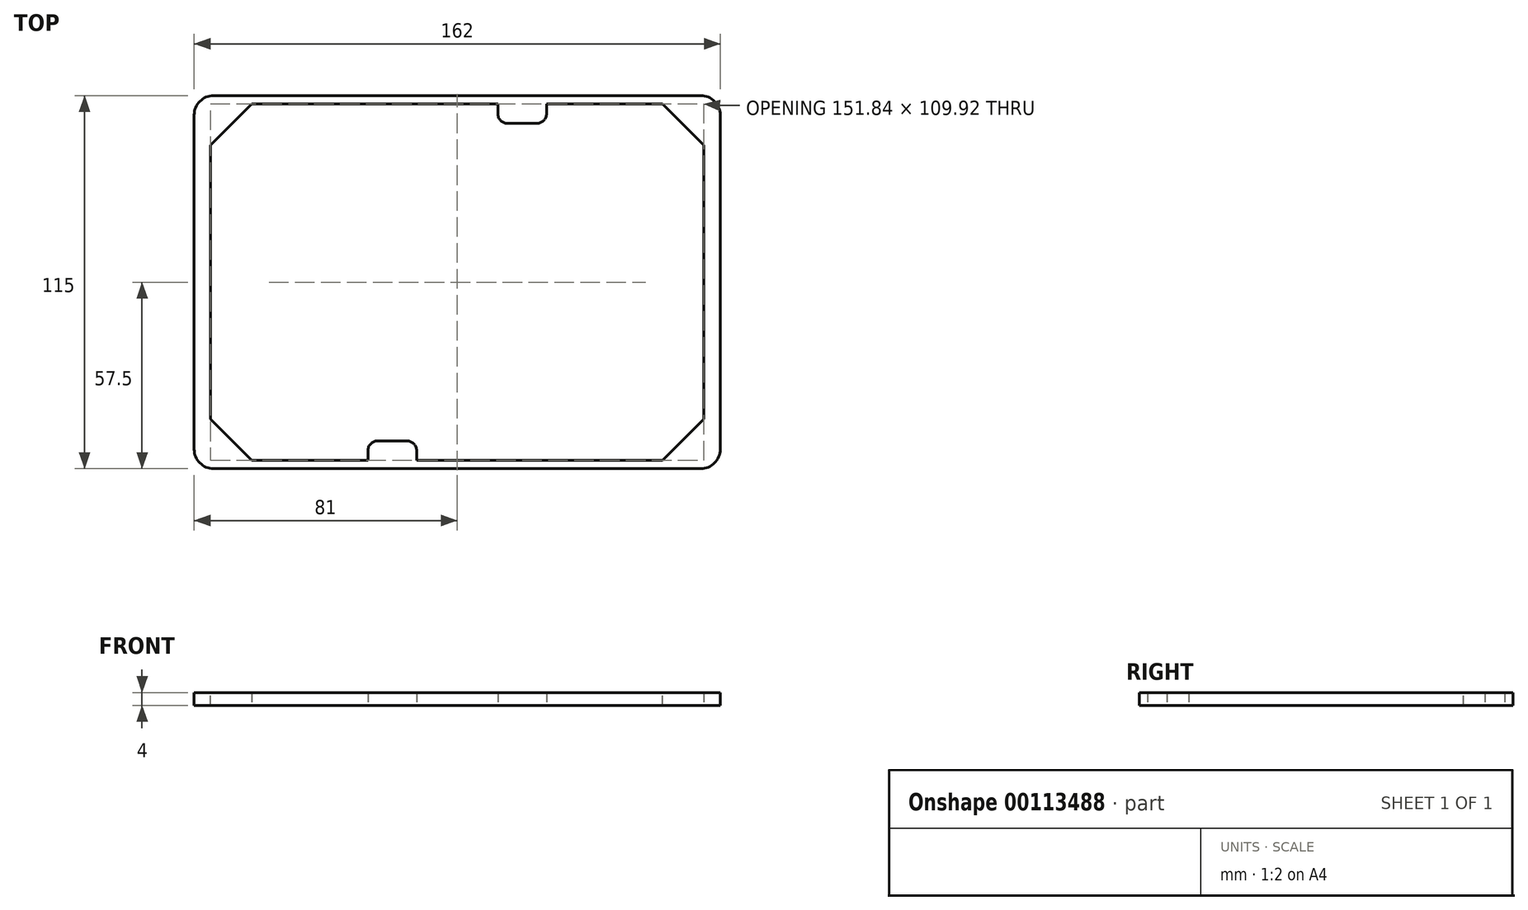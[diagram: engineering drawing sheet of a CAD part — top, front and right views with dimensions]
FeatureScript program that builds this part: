
annotation { "Feature Type Name" : "Feature", "Feature Type Description" : "" }
export const myFeature = defineFeature(function(context is Context, id is Id, definition is map)
    precondition{}
    {
        {
            var Q0;
            Q0=qCreatedBy(makeId("Top.planeOp"),FACE);
            var sketch = newSketch(context, id + "F0", { "sketchPlane" : qUnion([Q0])});
            skLineSegment(sketch, "E0.bottom", {"start": v(0, 0) * mm, "end": v(162, 0) * mm});
            skLineSegment(sketch, "E0.top", {"start": v(0, 115) * mm, "end": v(162, 115) * mm});
            skLineSegment(sketch, "E0.left", {"start": v(0, 0) * mm, "end": v(0, 115) * mm});
            skLineSegment(sketch, "E0.right", {"start": v(162, 0) * mm, "end": v(162, 115) * mm});
            skLineSegment(sketch, "E1.bottom", {"start": v(5.08, 112.46) * mm, "end": v(156.92, 112.46) * mm});
            skLineSegment(sketch, "E1.top", {"start": v(5.08, 2.54) * mm, "end": v(156.92, 2.54) * mm});
            skLineSegment(sketch, "E1.left", {"start": v(5.08, 112.46) * mm, "end": v(5.08, 2.54) * mm});
            skLineSegment(sketch, "E1.right", {"start": v(156.92, 112.46) * mm, "end": v(156.92, 2.54) * mm});
            skSolve(sketch);
        }
        {
            var Q0;
            Q0=qSketchRegion(id+"F0",true);
            extrude(context, id + "F1", {"entities" : qUnion([Q0]), "depth" : 4 * mm});
        }
        {
            var Q0;
            Q0=makeQuery(id+"F1.opExtrude","SWEPT_EDGE",EDGE,{"disambiguationData":[OSD([sQuery(id+"F0.wireOp",EDGE,"E0.top"),sQuery(id+"F0.wireOp",EDGE,"E0.left")])]});
            var Q1;
            Q1=makeQuery(id+"F1.opExtrude","SWEPT_EDGE",EDGE,{"disambiguationData":[OSD([sQuery(id+"F0.wireOp",EDGE,"E0.top"),sQuery(id+"F0.wireOp",EDGE,"E0.right")])]});
            var Q2;
            Q2=makeQuery(id+"F1.opExtrude","SWEPT_EDGE",EDGE,{"disambiguationData":[OSD([sQuery(id+"F0.wireOp",EDGE,"E0.bottom"),sQuery(id+"F0.wireOp",EDGE,"E0.right")])]});
            var Q3;
            Q3=makeQuery(id+"F1.opExtrude","SWEPT_EDGE",EDGE,{"disambiguationData":[OSD([sQuery(id+"F0.wireOp",EDGE,"E0.bottom"),sQuery(id+"F0.wireOp",EDGE,"E0.left")])]});
            fillet(context, id + "F2", {"entities" : qUnion([Q0, Q1, Q2, Q3]), "radius" : 6 * mm, "tangentPropagation" : true, "defaultsChanged" : false, "vertexSettings" : [], "allowEdgeOverflow" : false});
        }
        {
            var Q0;
            Q0=makeQuery(id+"F1.opExtrude","SWEPT_EDGE",EDGE,{"disambiguationData":[OSD([sQuery(id+"F0.wireOp",EDGE,"E1.bottom"),sQuery(id+"F0.wireOp",EDGE,"E1.left")])]});
            var Q1;
            Q1=makeQuery(id+"F1.opExtrude","SWEPT_EDGE",EDGE,{"disambiguationData":[OSD([sQuery(id+"F0.wireOp",EDGE,"E1.top"),sQuery(id+"F0.wireOp",EDGE,"E1.right")])]});
            var Q2;
            Q2=makeQuery(id+"F1.opExtrude","SWEPT_EDGE",EDGE,{"disambiguationData":[OSD([sQuery(id+"F0.wireOp",EDGE,"E1.bottom"),sQuery(id+"F0.wireOp",EDGE,"E1.right")])]});
            var Q3;
            Q3=makeQuery(id+"F1.opExtrude","SWEPT_EDGE",EDGE,{"disambiguationData":[OSD([sQuery(id+"F0.wireOp",EDGE,"E1.top"),sQuery(id+"F0.wireOp",EDGE,"E1.left")])]});
            chamfer(context, id + "F3", {"entities" : qUnion([Q0, Q1, Q2, Q3]), "width" : 12.7 * mm, "tangentPropagation" : true});
        }
        {
            var Q0;
            Q0=makeQuery(id+"F1.opExtrude","SWEPT_FACE",FACE,{"disambiguationData":[OSD([sQuery(id+"F0.wireOp",EDGE,"E1.top")])]});
            var sketch = newSketch(context, id + "F4", { "sketchPlane" : qUnion([Q0])});
            skLineSegment(sketch, "E2.bottom", {"start": v(-68.5, 4) * mm, "end": v(-53.5, 4) * mm});
            skLineSegment(sketch, "E2.top", {"start": v(-68.5, 0) * mm, "end": v(-53.5, 0) * mm});
            skLineSegment(sketch, "E2.left", {"start": v(-68.5, 4) * mm, "end": v(-68.5, 0) * mm});
            skLineSegment(sketch, "E2.right", {"start": v(-53.5, 4) * mm, "end": v(-53.5, 0) * mm});
            skSolve(sketch);
        }
        {
            var Q0;
            Q0 = qSketchRegion(id + "F4", true);
            extrude(context, id + "F5", {"entities" : qUnion([Q0]), "operationType" : NewBodyOperationType.ADD, "depth" : 6 * mm, "offsetDistance" : 25 * mm});
        }
        {
            var Q0;
            Q0=makeQuery(id+"F1.opExtrude","SWEPT_FACE",FACE,{"disambiguationData":[OSD([sQuery(id+"F0.wireOp",EDGE,"E1.bottom")])]});
            var sketch = newSketch(context, id + "F6", { "sketchPlane" : qUnion([Q0])});
            skLineSegment(sketch, "E3.bottom", {"start": v(93.5, 4) * mm, "end": v(108.5, 4) * mm});
            skLineSegment(sketch, "E3.top", {"start": v(93.5, 0) * mm, "end": v(108.5, 0) * mm});
            skLineSegment(sketch, "E3.left", {"start": v(93.5, 4) * mm, "end": v(93.5, 0) * mm});
            skLineSegment(sketch, "E3.right", {"start": v(108.5, 4) * mm, "end": v(108.5, 0) * mm});
            skSolve(sketch);
        }
        {
            var Q0;
            Q0 = qSketchRegion(id + "F6", true);
            extrude(context, id + "F7", {"entities" : qUnion([Q0]), "operationType" : NewBodyOperationType.ADD, "depth" : 6 * mm, "offsetDistance" : 25 * mm});
        }
        {
            var Q0;
            Q0=makeQuery(id+"F7.opExtrude","CAP_EDGE",EDGE,{"disambiguationData":[OSD([sQuery(id+"F6.wireOp",EDGE,"E3.left")])],"isStart":false});
            var Q1;
            Q1=makeQuery(id+"F7.opExtrude","CAP_EDGE",EDGE,{"disambiguationData":[OSD([sQuery(id+"F6.wireOp",EDGE,"E3.right")])],"isStart":false});
            var Q2;
            Q2=makeQuery(id+"F5.opExtrude","CAP_EDGE",EDGE,{"disambiguationData":[OSD([sQuery(id+"F4.wireOp",EDGE,"E2.left")])],"isStart":false});
            var Q3;
            Q3=makeQuery(id+"F5.opExtrude","CAP_EDGE",EDGE,{"disambiguationData":[OSD([sQuery(id+"F4.wireOp",EDGE,"E2.right")])],"isStart":false});
            fillet(context, id + "F8", {"entities" : qUnion([Q0, Q1, Q2, Q3]), "tangentPropagation" : true, "radius" : 3 * mm, "defaultsChanged" : true, "vertexSettings" : [], "allowEdgeOverflow" : false});
        }
    });
